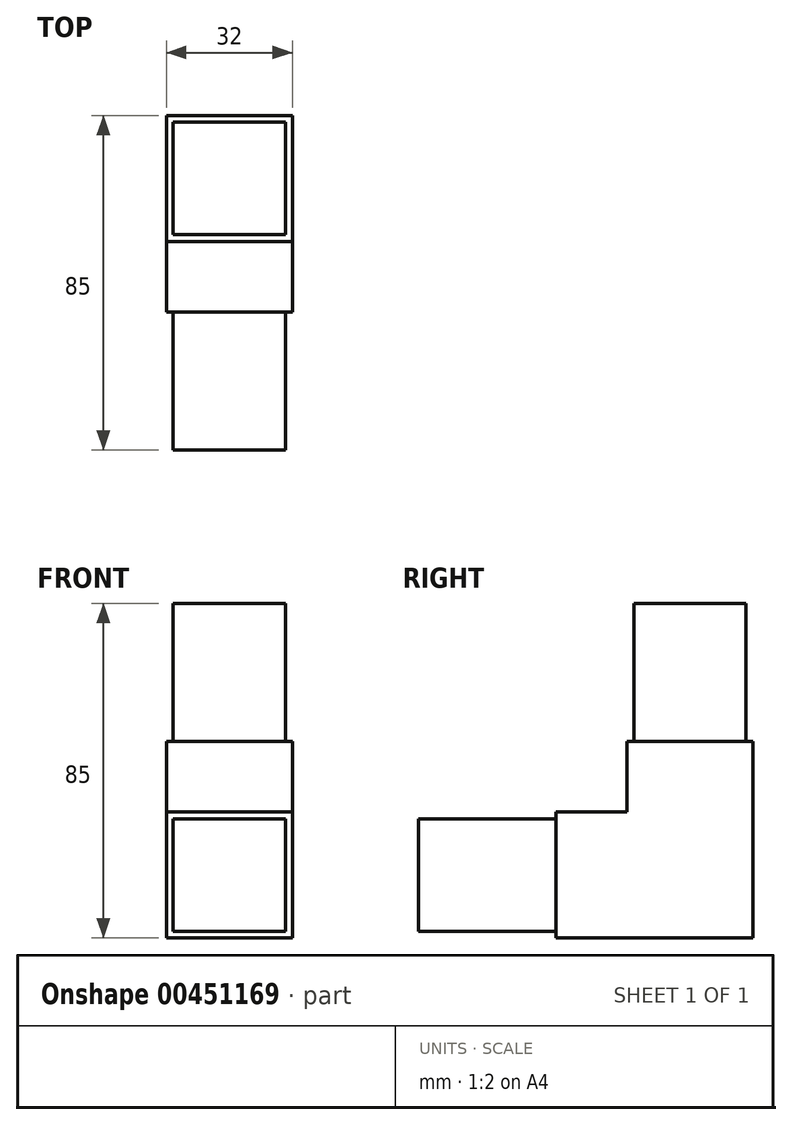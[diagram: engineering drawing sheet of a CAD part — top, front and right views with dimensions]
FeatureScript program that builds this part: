
annotation { "Feature Type Name" : "Feature", "Feature Type Description" : "" }
export const myFeature = defineFeature(function(context is Context, id is Id, definition is map)
    precondition{}
    {
        {
            var Q0;
            Q0=qCreatedBy(makeId("Front.planeOp"),FACE);
            var sketch = newSketch(context, id + "F0", { "sketchPlane" : qUnion([Q0])});
            skLineSegment(sketch, "E0.bottom", {"start": v(16, -16) * mm, "end": v(-16, -16) * mm});
            skLineSegment(sketch, "E0.top", {"start": v(16, 16) * mm, "end": v(-16, 16) * mm});
            skLineSegment(sketch, "E0.left", {"start": v(16, -16) * mm, "end": v(16, 16) * mm});
            skLineSegment(sketch, "E0.right", {"start": v(-16, -16) * mm, "end": v(-16, 16) * mm});
            skPoint(sketch, "E0.middle", {"position": v(0, 0) * mm});
            skSolve(sketch);
        }
        {
            var Q0;
            Q0=qSketchRegion(id+"F0",true);
            extrude(context, id + "F1", {"entities" : qUnion([Q0]), "depth" : 32 * mm, "offsetDistance" : 25 * mm});
        }
        {
            var Q0;
            Q0=makeQuery(id+"F1.opExtrude","SWEPT_FACE",FACE,{"disambiguationData":[OSD([sQuery(id+"F0.wireOp",EDGE,"E0.top")])]});
            var sketch = newSketch(context, id + "F2", { "sketchPlane" : qUnion([Q0])});
            skLineSegment(sketch, "E1.bottom", {"start": v(-16, 0) * mm, "end": v(16, 0) * mm});
            skLineSegment(sketch, "E1.top", {"start": v(-16, -32) * mm, "end": v(16, -32) * mm});
            skLineSegment(sketch, "E1.left", {"start": v(-16, 0) * mm, "end": v(-16, -32) * mm});
            skLineSegment(sketch, "E1.right", {"start": v(16, 0) * mm, "end": v(16, -32) * mm});
            skSolve(sketch);
        }
        {
            var Q0;
            Q0=qSketchRegion(id+"F2",true);
            extrude(context, id + "F3", {"entities" : qUnion([Q0]), "operationType" : NewBodyOperationType.ADD, "depth" : 18 * mm, "offsetDistance" : 25 * mm});
        }
        {
            var Q0;
            Q0=makeQuery(id+"F3.boolean.opBoolean","MERGE",FACE,{"derivedFrom":[makeQuery(id+"F1.opExtrude","CAP_FACE",FACE,{"disambiguationData":[OSD([sQuery(id+"F0.wireOp",EDGE,"E0.bottom"),sQuery(id+"F0.wireOp",EDGE,"E0.top"),sQuery(id+"F0.wireOp",EDGE,"E0.left"),sQuery(id+"F0.wireOp",EDGE,"E0.right")])],"isStart":false}),makeQuery(id+"F3.opExtrude","SWEPT_FACE",FACE,{"disambiguationData":[OSD([sQuery(id+"F2.wireOp",EDGE,"E1.top")])]})]});
            var sketch = newSketch(context, id + "F4", { "sketchPlane" : qUnion([Q0])});
            skLineSegment(sketch, "E2.bottom", {"start": v(-16, -16) * mm, "end": v(16, -16) * mm});
            skLineSegment(sketch, "E2.top", {"start": v(-16, 16) * mm, "end": v(16, 16) * mm});
            skLineSegment(sketch, "E2.left", {"start": v(-16, -16) * mm, "end": v(-16, 16) * mm});
            skLineSegment(sketch, "E2.right", {"start": v(16, -16) * mm, "end": v(16, 16) * mm});
            skSolve(sketch);
        }
        {
            var Q0;
            Q0=qSketchRegion(id+"F4",true);
            extrude(context, id + "F5", {"entities" : qUnion([Q0]), "operationType" : NewBodyOperationType.ADD, "depth" : 18 * mm, "offsetDistance" : 25 * mm});
        }
        {
            var Q0;
            Q0=makeQuery(id+"F3.opExtrude","CAP_FACE",FACE,{"disambiguationData":[OSD([sQuery(id+"F2.wireOp",EDGE,"E1.bottom"),sQuery(id+"F2.wireOp",EDGE,"E1.top"),sQuery(id+"F2.wireOp",EDGE,"E1.left"),sQuery(id+"F2.wireOp",EDGE,"E1.right")])],"isStart":false});
            var sketch = newSketch(context, id + "F6", { "sketchPlane" : qUnion([Q0])});
            skLineSegment(sketch, "E3.bottom", {"start": v(-14.25, -30.25) * mm, "end": v(14.25, -30.25) * mm});
            skLineSegment(sketch, "E3.top", {"start": v(-14.25, -1.75) * mm, "end": v(14.25, -1.75) * mm});
            skLineSegment(sketch, "E3.left", {"start": v(-14.25, -30.25) * mm, "end": v(-14.25, -1.75) * mm});
            skLineSegment(sketch, "E3.right", {"start": v(14.25, -30.25) * mm, "end": v(14.25, -1.75) * mm});
            skPoint(sketch, "E3.middle", {"position": v(0, -16) * mm});
            skPoint(sketch, "E3.middle.positionSnap0", {"position": v(16, -16) * mm});
            skPoint(sketch, "E3.centerSnap0", {"position": v(16, -16) * mm});
            skSolve(sketch);
        }
        {
            var Q0;
            Q0=qSketchRegion(id+"F6",true);
            extrude(context, id + "F7", {"entities" : qUnion([Q0]), "operationType" : NewBodyOperationType.ADD, "depth" : 35 * mm, "offsetDistance" : 25 * mm});
        }
        {
            var Q0;
            Q0=makeQuery(id+"F5.opExtrude","CAP_FACE",FACE,{"disambiguationData":[OSD([sQuery(id+"F4.wireOp",EDGE,"E2.bottom"),sQuery(id+"F4.wireOp",EDGE,"E2.top"),sQuery(id+"F4.wireOp",EDGE,"E2.left"),sQuery(id+"F4.wireOp",EDGE,"E2.right")])],"isStart":false});
            var sketch = newSketch(context, id + "F8", { "sketchPlane" : qUnion([Q0])});
            skLineSegment(sketch, "E4.bottom", {"start": v(14.25, -14.25) * mm, "end": v(-14.25, -14.25) * mm});
            skLineSegment(sketch, "E4.top", {"start": v(14.25, 14.25) * mm, "end": v(-14.25, 14.25) * mm});
            skLineSegment(sketch, "E4.left", {"start": v(14.25, -14.25) * mm, "end": v(14.25, 14.25) * mm});
            skLineSegment(sketch, "E4.right", {"start": v(-14.25, -14.25) * mm, "end": v(-14.25, 14.25) * mm});
            skPoint(sketch, "E4.middle", {"position": v(0, 0) * mm});
            skSolve(sketch);
        }
        {
            var Q0;
            Q0=qSketchRegion(id+"F8",true);
            extrude(context, id + "F9", {"entities" : qUnion([Q0]), "operationType" : NewBodyOperationType.ADD, "depth" : 35 * mm, "offsetDistance" : 25 * mm});
        }
    });
